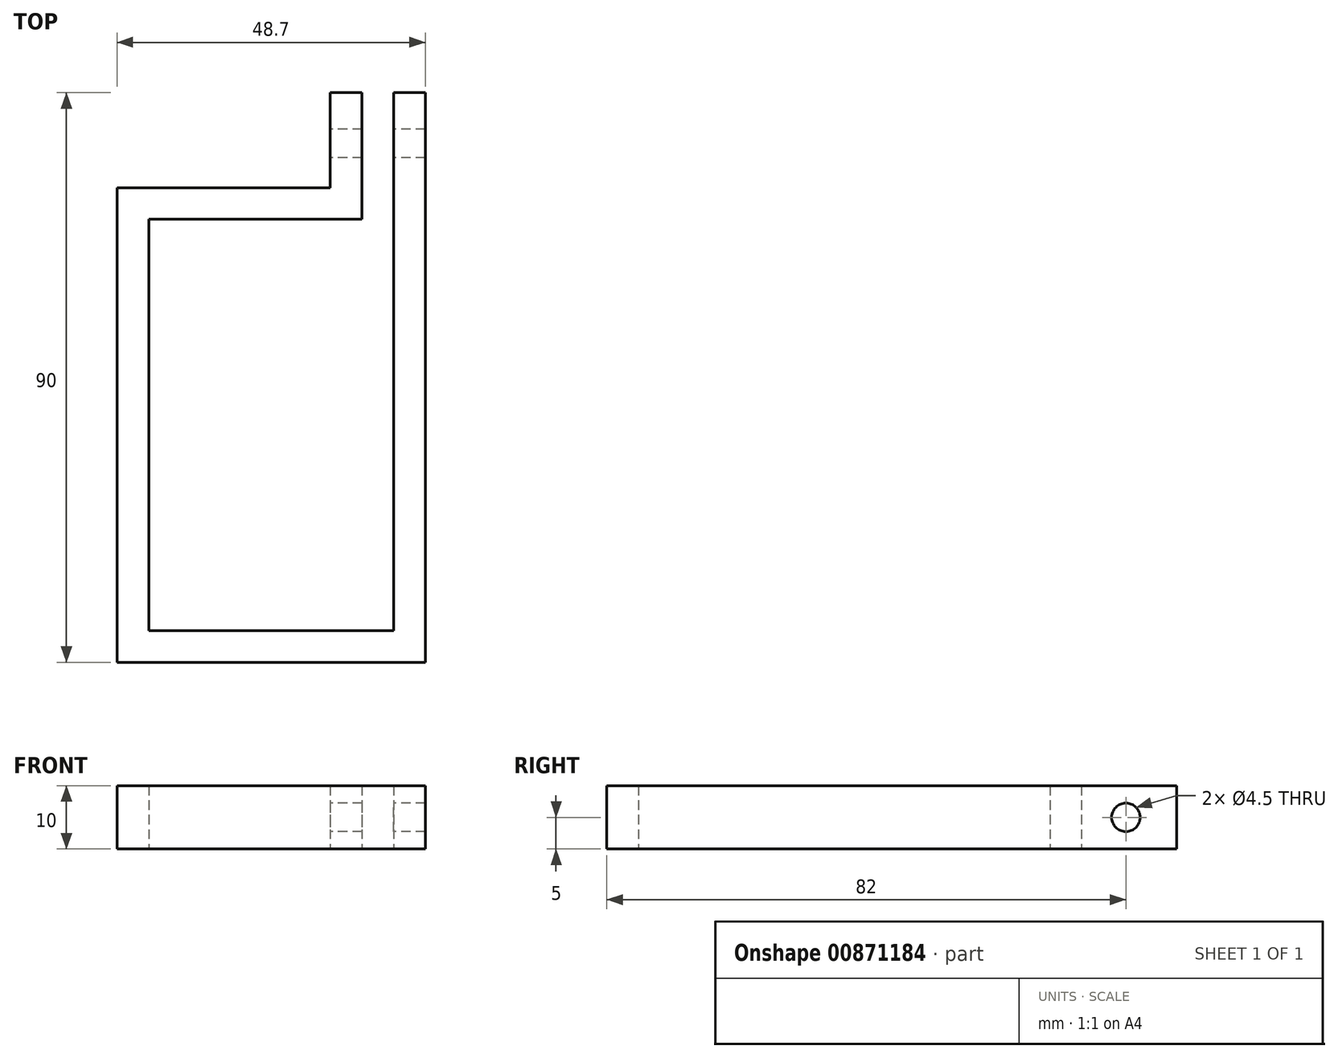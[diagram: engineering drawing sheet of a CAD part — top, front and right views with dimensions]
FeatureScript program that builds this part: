
annotation { "Feature Type Name" : "Feature", "Feature Type Description" : "" }
export const myFeature = defineFeature(function(context is Context, id is Id, definition is map)
    precondition{}
    {
        {
            var Q0;
            Q0=qCreatedBy(makeId("Top.planeOp"),FACE);
            var sketch = newSketch(context, id + "F0", { "sketchPlane" : qUnion([Q0])});
            skLineSegment(sketch, "E0", {"start": v(0, 0) * mm, "end": v(48.7, 0) * mm});
            skLineSegment(sketch, "E1", {"start": v(48.7, 0) * mm, "end": v(48.7, 90) * mm});
            skLineSegment(sketch, "E2", {"start": v(48.7, 90) * mm, "end": v(43.7, 90) * mm});
            skLineSegment(sketch, "E3", {"start": v(43.7, 90) * mm, "end": v(43.7, 5) * mm});
            skLineSegment(sketch, "E4", {"start": v(43.7, 5) * mm, "end": v(5, 5) * mm});
            skLineSegment(sketch, "E5", {"start": v(5, 5) * mm, "end": v(5, 70) * mm});
            skLineSegment(sketch, "E6", {"start": v(5, 70) * mm, "end": v(38.7, 70) * mm});
            skLineSegment(sketch, "E7", {"start": v(38.7, 70) * mm, "end": v(38.7, 90) * mm});
            skLineSegment(sketch, "E8", {"start": v(38.7, 90) * mm, "end": v(33.7, 90) * mm});
            skLineSegment(sketch, "E9", {"start": v(33.7, 90) * mm, "end": v(33.7, 75) * mm});
            skLineSegment(sketch, "E10", {"start": v(33.7, 75) * mm, "end": v(0, 75) * mm});
            skLineSegment(sketch, "E11", {"start": v(0, 75) * mm, "end": v(0, 0) * mm});
            skSolve(sketch);
        }
        {
            var Q0;
            Q0=makeQuery(id+"F0.imprint","IMPRINT",FACE,{"disambiguationData":[TD([[makeQuery(id+"F0.imprint","IMPRINT",EDGE,{"derivedFrom":sQuery(id+"F0.wireOp",EDGE,"E0")}),1.0]])]});
            extrude(context, id + "F1", {"entities" : qUnion([Q0]), "depth" : 10 * mm, "offsetDistance" : 25 * mm});
        }
        {
            var Q0;
            Q0=makeQuery(id+"F1.opExtrude","SWEPT_FACE",FACE,{"disambiguationData":[OSD([sQuery(id+"F0.wireOp",EDGE,"E9")])]});
            var sketch = newSketch(context, id + "F2", { "sketchPlane" : qUnion([Q0])});
            skCircle(sketch, "E12", {"center": v(-82, 5) * mm, "radius": 2.25 * mm});
            skSolve(sketch);
        }
        {
            var Q0;
            Q0 = qSketchRegion(id + "F2", true);
            extrude(context, id + "F3", {"entities" : qUnion([Q0]), "operationType" : NewBodyOperationType.REMOVE, "endBound" : BoundingType.THROUGH_ALL, "oppositeDirection" : true, "depth" : 25 * mm, "offsetDistance" : 25 * mm});
        }
    });
